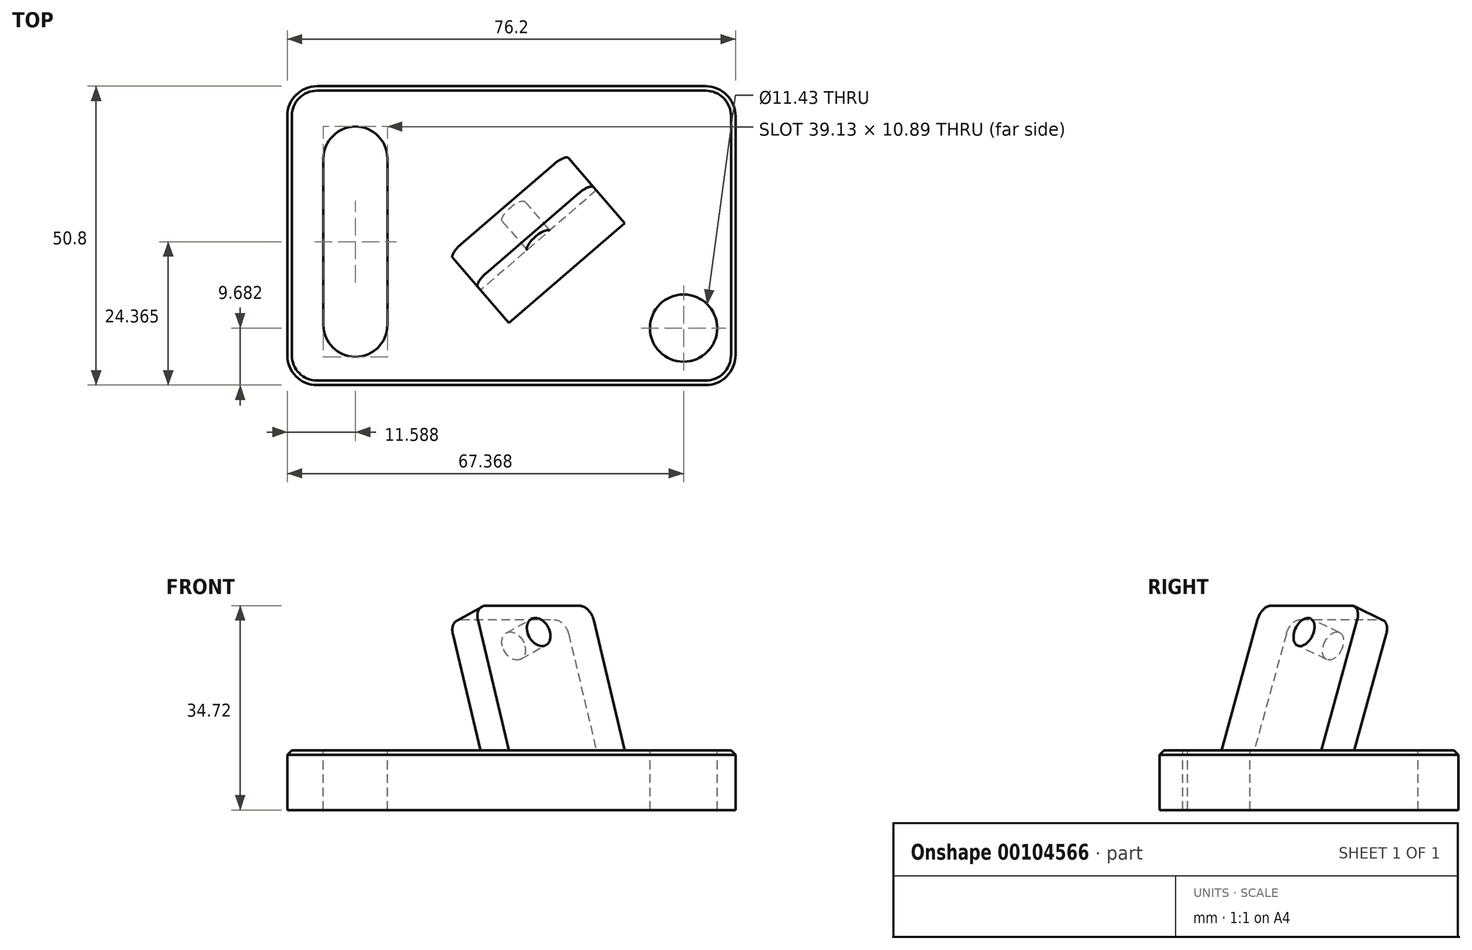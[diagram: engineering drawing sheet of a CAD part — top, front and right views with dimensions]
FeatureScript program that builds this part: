
annotation { "Feature Type Name" : "Feature", "Feature Type Description" : "" }
export const myFeature = defineFeature(function(context is Context, id is Id, definition is map)
    precondition{}
    {
        {
            var Q0;
            Q0=qCreatedBy(makeId("Top.planeOp"),FACE);
            var sketch = newSketch(context, id + "F0", { "sketchPlane" : qUnion([Q0])});
            skLineSegment(sketch, "E0", {"start": v(-38.4, 0) * mm, "end": v(-38.4, 50.8) * mm});
            skLineSegment(sketch, "E1", {"start": v(-38.4, 50.8) * mm, "end": v(37.8, 50.8) * mm});
            skLineSegment(sketch, "E2", {"start": v(37.8, 50.8) * mm, "end": v(37.8, 0) * mm});
            skLineSegment(sketch, "E3", {"start": v(37.8, 0) * mm, "end": v(-38.4, 0) * mm});
            skSolve(sketch);
        }
        {
            var Q0;
            Q0 = qSketchRegion(id + "F0", true);
            extrude(context, id + "F1", {"entities" : qUnion([Q0]), "depth" : 10.16 * mm});
        }
        {
            var Q0;
            Q0=makeQuery(id+"F1.opExtrude","CAP_FACE",FACE,{"disambiguationData":[OSD([sQuery(id+"F0.wireOp",EDGE,"E0"),sQuery(id+"F0.wireOp",EDGE,"E1"),sQuery(id+"F0.wireOp",EDGE,"E2"),sQuery(id+"F0.wireOp",EDGE,"E3")])],"isStart":false});
            var sketch = newSketch(context, id + "F2", { "sketchPlane" : qUnion([Q0])});
            skLineSegment(sketch, "E4", {"start": v(-5.55, 16.13) * mm, "end": v(14.15, 33.1) * mm});
            skSolve(sketch);
        }
        {
            var Q0;
            Q0=sQuery(id+"F2.wireOp",EDGE,"E4");
            var Q1;
            Q1=makeQuery(id+"F2.imprint","IMPRINT",FACE,{"disambiguationData":[TD([[makeQuery(id+"F2.imprint","IMPRINT",EDGE,{"derivedFrom":makeQuery(id+"F1.opExtrude","CAP_EDGE",EDGE,{"disambiguationData":[OSD([sQuery(id+"F0.wireOp",EDGE,"E0")])],"isStart":false})}),-1.0]])]});
            cPlane(context, id + "F3", {"entities" : qUnion([Q0, Q1]), "cplaneType" : CPlaneType.LINE_ANGLE, "offset" : 25.4 * mm, "angle" : 160 * degree, "width" : 152.4 * mm, "height" : 152.4 * mm});
        }
        {
            var Q0;
            Q0=qCreatedBy(id+"F3.planeOp",FACE);
            var sketch = newSketch(context, id + "F4", { "sketchPlane" : qUnion([Q0])});
            skLineSegment(sketch, "E5.0", {"start": v(-2.26, 12.85) * mm, "end": v(17.94, 29.21) * mm});
            skLineSegment(sketch, "E6", {"start": v(17.94, 29.21) * mm, "end": v(22.3, 23.83) * mm});
            skLineSegment(sketch, "E7", {"start": v(22.3, 23.83) * mm, "end": v(2.1, 7.46) * mm});
            skLineSegment(sketch, "E8", {"start": v(2.1, 7.46) * mm, "end": v(-2.26, 12.85) * mm});
            skSolve(sketch);
        }
        {
            var Q0;
            Q0 = qSketchRegion(id + "F4", true);
            extrude(context, id + "F5", {"entities" : qUnion([Q0]), "operationType" : NewBodyOperationType.ADD, "depth" : 23.6 * mm, "hasSecondDirection" : true, "secondDirectionOppositeDirection" : true, "secondDirectionDepth" : 6 * mm});
        }
        {
            var Q0;
            Q0=makeQuery(id+"F2.imprint","IMPRINT",FACE,{"disambiguationData":[TD([[makeQuery(id+"F2.imprint","IMPRINT",EDGE,{"derivedFrom":makeQuery(id+"F1.opExtrude","CAP_EDGE",EDGE,{"disambiguationData":[OSD([sQuery(id+"F0.wireOp",EDGE,"E0")])],"isStart":false})}),-1.0]])]});
            var sketch = newSketch(context, id + "F6", { "sketchPlane" : qUnion([Q0])});
            skLineSegment(sketch, "E9.0", {"start": v(-38.4, 0) * mm, "end": v(-38.4, 50.8) * mm});
            skLineSegment(sketch, "E10", {"start": v(-32.25, 38.48) * mm, "end": v(-32.25, 10.25) * mm});
            skLineSegment(sketch, "E11", {"start": v(-21.36, 10.25) * mm, "end": v(-21.36, 38.48) * mm});
            skArc(sketch, "E12", {"start": v(-32.25, 38.48) * mm, "mid": v(-26.8, 43.93) * mm, "end": v(-21.36, 38.48) * mm});
            skArc(sketch, "E13", {"start": v(-32.25, 10.25) * mm, "mid": v(-26.8, 4.8) * mm, "end": v(-21.36, 10.25) * mm});
            skSolve(sketch);
        }
        {
            var Q0;
            Q0 = qSketchRegion(id + "F6", true);
            extrude(context, id + "F7", {"entities" : qUnion([Q0]), "operationType" : NewBodyOperationType.REMOVE, "oppositeDirection" : true, "depth" : 25.4 * mm});
        }
        {
            var Q0;
            Q0=makeQuery(id+"F2.imprint","IMPRINT",FACE,{"disambiguationData":[TD([[makeQuery(id+"F2.imprint","IMPRINT",EDGE,{"derivedFrom":makeQuery(id+"F1.opExtrude","CAP_EDGE",EDGE,{"disambiguationData":[OSD([sQuery(id+"F0.wireOp",EDGE,"E0")])],"isStart":false})}),-1.0]])]});
            var sketch = newSketch(context, id + "F8", { "sketchPlane" : qUnion([Q0])});
            skPoint(sketch, "E14", {"position": v(28.98, 9.68) * mm});
            skSolve(sketch);
        }
        {
            var Q0;
            Q0=sQuery(id+"F8.wireOp",VERTEX,"E14");
            var Q1;
            Q1=makeQuery(id+"F1.opExtrude","SWEPT_BODY",BODY,{"disambiguationData":[OSD([sQuery(id+"F0.wireOp",EDGE,"E0"),sQuery(id+"F0.wireOp",EDGE,"E1"),sQuery(id+"F0.wireOp",EDGE,"E2"),sQuery(id+"F0.wireOp",EDGE,"E3")])]});
            hole(context, id + "F9", {"style" : HoleStyle.SIMPLE, "endStyle" : HoleEndStyle.BLIND, "holeDiameter" : 11.43 * mm, "holeDepth" : 127 * mm, "locations" : qUnion([Q0]), "scope" : qUnion([Q1])});
        }
        {
            var Q0;
            Q0=makeQuery(id+"F5.opExtrude","SWEPT_FACE",FACE,{"disambiguationData":[OSD([sQuery(id+"F4.wireOp",EDGE,"E7")])]});
            var sketch = newSketch(context, id + "F10", { "sketchPlane" : qUnion([Q0])});
            skPoint(sketch, "E15", {"position": v(8.98, 37.9) * mm});
            skLineSegment(sketch, "E16", {"start": v(-3.41, 33.95) * mm, "end": v(21.53, 41.3) * mm});
            skSolve(sketch);
        }
        {
            var Q0;
            Q0=sQuery(id+"F10.wireOp",VERTEX,"E15");
            var Q1;
            Q1=makeQuery(id+"F1.opExtrude","SWEPT_BODY",BODY,{"disambiguationData":[OSD([sQuery(id+"F0.wireOp",EDGE,"E0"),sQuery(id+"F0.wireOp",EDGE,"E1"),sQuery(id+"F0.wireOp",EDGE,"E2"),sQuery(id+"F0.wireOp",EDGE,"E3")])]});
            hole(context, id + "F11", {"style" : HoleStyle.SIMPLE, "endStyle" : HoleEndStyle.BLIND, "holeDiameter" : 5.08 * mm, "holeDepth" : 127 * mm, "locations" : qUnion([Q0]), "scope" : qUnion([Q1])});
        }
        {
            var Q0;
            Q0=makeQuery(id+"F1.opExtrude","SWEPT_EDGE",EDGE,{"disambiguationData":[OSD([sQuery(id+"F0.wireOp",EDGE,"E2"),sQuery(id+"F0.wireOp",EDGE,"E3")])]});
            var Q1;
            Q1=makeQuery(id+"F1.opExtrude","SWEPT_EDGE",EDGE,{"disambiguationData":[OSD([sQuery(id+"F0.wireOp",EDGE,"E1"),sQuery(id+"F0.wireOp",EDGE,"E2")])]});
            var Q2;
            Q2=makeQuery(id+"F1.opExtrude","SWEPT_EDGE",EDGE,{"disambiguationData":[OSD([sQuery(id+"F0.wireOp",EDGE,"E0"),sQuery(id+"F0.wireOp",EDGE,"E1")])]});
            var Q3;
            Q3=makeQuery(id+"F1.opExtrude","SWEPT_EDGE",EDGE,{"disambiguationData":[OSD([sQuery(id+"F0.wireOp",EDGE,"E0"),sQuery(id+"F0.wireOp",EDGE,"E3")])]});
            fillet(context, id + "F12", {"entities" : qUnion([Q0, Q1, Q2, Q3]), "radius" : 5.08 * mm, "tangentPropagation" : true, "allowEdgeOverflow" : false});
        }
        {
            var Q0;
            Q0=makeQuery(id+"F1.opExtrude","CAP_EDGE",EDGE,{"disambiguationData":[OSD([sQuery(id+"F0.wireOp",EDGE,"E3")])],"isStart":false});
            chamfer(context, id + "F13", {"entities" : qUnion([Q0]), "width" : 0.76 * mm, "tangentPropagation" : true});
        }
        {
            var Q0;
            Q0=makeQuery(id+"F5.opExtrude","CAP_EDGE",EDGE,{"disambiguationData":[OSD([sQuery(id+"F4.wireOp",EDGE,"E8")])],"isStart":false});
            var Q1;
            Q1=makeQuery(id+"F5.opExtrude","CAP_EDGE",EDGE,{"disambiguationData":[OSD([sQuery(id+"F4.wireOp",EDGE,"E6")])],"isStart":false});
            fillet(context, id + "F14", {"entities" : qUnion([Q0, Q1]), "radius" : 2.54 * mm, "tangentPropagation" : true, "allowEdgeOverflow" : false});
        }
    });
